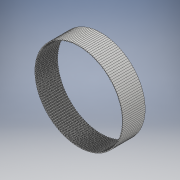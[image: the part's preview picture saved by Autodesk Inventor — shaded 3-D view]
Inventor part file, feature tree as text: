
AUTODESK INVENTOR PART (.ipt)
format: ipt  version: 2019 (Build 230136000, 136)  size: 10,706,944 bytes
history: native  units: in
note: dims shown in document units (in); Inventor stores cm internally (conversion verified against a paired STEP export)
features: other x4, extrude x1, sketch x1
ambient origin geometry x8: Origin, YZ Plane, XZ Plane, XY Plane, X Axis, Y Axis, Z Axis, Center Point
bodies: Solid1 (feature_tree)
feature tree (6):
  other  "XLbelt"
  other  "Repaired Geometry1"
  extrude  "Extrusion1"  [1 undecoded]
  sketch  "Sketch1"  dims[d0=2.4444in d1=0.0in]
  other  "Composite1"
  other  "Srf1"
note: 1 required parameter value undecoded (feature->parameter linkage not recoverable at this tier; creation-order binding heuristic only, values carry confidence <= 0.55)
